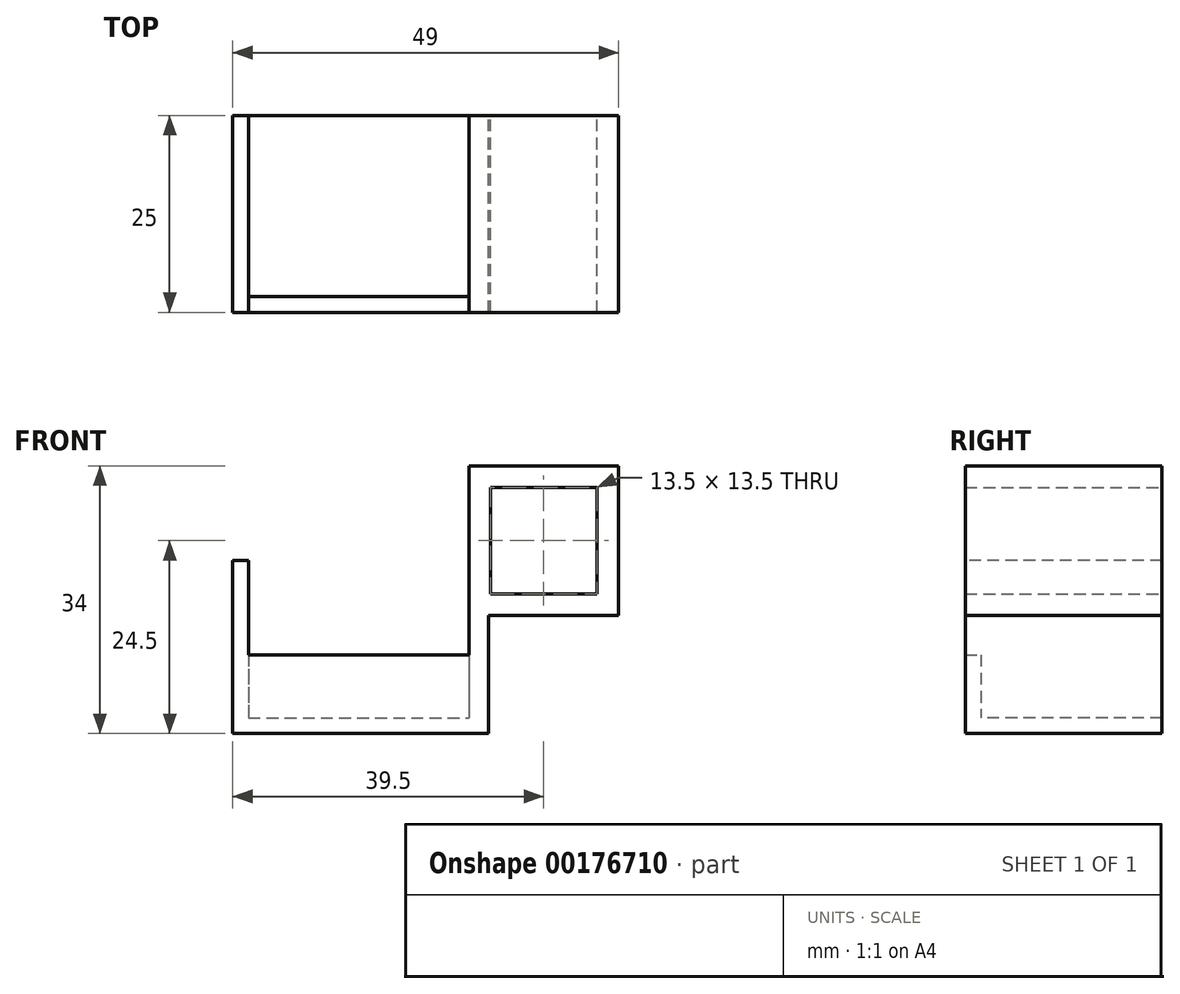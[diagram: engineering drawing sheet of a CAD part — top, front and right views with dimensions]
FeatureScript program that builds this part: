
annotation { "Feature Type Name" : "Feature", "Feature Type Description" : "" }
export const myFeature = defineFeature(function(context is Context, id is Id, definition is map)
    precondition{}
    {
        {
            var Q0;
            Q0=qCreatedBy(makeId("Front.planeOp"),FACE);
            var sketch = newSketch(context, id + "F0", { "sketchPlane" : qUnion([Q0])});
            skLineSegment(sketch, "E0.bottom", {"start": v(9.5, 9.5) * mm, "end": v(-9.5, 9.5) * mm});
            skLineSegment(sketch, "E0.top", {"start": v(9.5, -9.5) * mm, "end": v(-9.5, -9.5) * mm});
            skLineSegment(sketch, "E0.left", {"start": v(9.5, 9.5) * mm, "end": v(9.5, -9.5) * mm});
            skLineSegment(sketch, "E0.right", {"start": v(-9.5, 9.5) * mm, "end": v(-9.5, -9.5) * mm});
            skPoint(sketch, "E0.middle", {"position": v(0, 0) * mm});
            skLineSegment(sketch, "E1.bottom", {"start": v(6.75, 6.75) * mm, "end": v(-6.75, 6.75) * mm});
            skLineSegment(sketch, "E1.top", {"start": v(6.75, -6.75) * mm, "end": v(-6.75, -6.75) * mm});
            skLineSegment(sketch, "E1.left", {"start": v(6.75, 6.75) * mm, "end": v(6.75, -6.75) * mm});
            skLineSegment(sketch, "E1.right", {"start": v(-6.75, 6.75) * mm, "end": v(-6.75, -6.75) * mm});
            skSolve(sketch);
        }
        {
            var Q0;
            Q0 = qSketchRegion(id + "F0", true);
            extrude(context, id + "F1", {"entities" : qUnion([Q0]), "endBound" : BoundingType.SYMMETRIC, "depth" : 25 * mm});
        }
        {
            var Q0;
            Q0=makeQuery(id+"F1.opExtrude","SWEPT_FACE",FACE,{"disambiguationData":[OSD([sQuery(id+"F0.wireOp",EDGE,"E0.right")])]});
            var sketch = newSketch(context, id + "F2", { "sketchPlane" : qUnion([Q0])});
            skLineSegment(sketch, "E2.bottom", {"start": v(-12.5, 9.5) * mm, "end": v(12.5, 9.5) * mm});
            skLineSegment(sketch, "E2.top", {"start": v(-12.5, -24.5) * mm, "end": v(12.5, -24.5) * mm});
            skLineSegment(sketch, "E2.left", {"start": v(-12.5, 9.5) * mm, "end": v(-12.5, -24.5) * mm});
            skLineSegment(sketch, "E2.right", {"start": v(12.5, 9.5) * mm, "end": v(12.5, -24.5) * mm});
            skSolve(sketch);
        }
        {
            var Q0;
            Q0 = qSketchRegion(id + "F2", true);
            extrude(context, id + "F3", {"entities" : qUnion([Q0]), "operationType" : NewBodyOperationType.ADD, "oppositeDirection" : true, "depth" : 2.5 * mm});
        }
        {
            var Q0;
            Q0=makeQuery(id+"F3.boolean.opBoolean","MERGE",FACE,{"derivedFrom":[makeQuery(id+"F1.opExtrude","SWEPT_FACE",FACE,{"disambiguationData":[OSD([sQuery(id+"F0.wireOp",EDGE,"E0.right")])]}),makeQuery(id+"F3.opExtrude","CAP_FACE",FACE,{"disambiguationData":[OSD([sQuery(id+"F2.wireOp",EDGE,"E2.bottom"),sQuery(id+"F2.wireOp",EDGE,"E2.top"),sQuery(id+"F2.wireOp",EDGE,"E2.left"),sQuery(id+"F2.wireOp",EDGE,"E2.right")])],"isStart":true})]});
            var sketch = newSketch(context, id + "F4", { "sketchPlane" : qUnion([Q0])});
            skLineSegment(sketch, "E3.bottom", {"start": v(-12.5, -24.5) * mm, "end": v(12.5, -24.5) * mm});
            skLineSegment(sketch, "E3.top", {"start": v(-12.5, -22.5) * mm, "end": v(12.5, -22.5) * mm});
            skLineSegment(sketch, "E3.left", {"start": v(-12.5, -24.5) * mm, "end": v(-12.5, -22.5) * mm});
            skLineSegment(sketch, "E3.right", {"start": v(12.5, -24.5) * mm, "end": v(12.5, -22.5) * mm});
            skSolve(sketch);
        }
        {
            var Q0;
            Q0 = qSketchRegion(id + "F4", true);
            extrude(context, id + "F5", {"entities" : qUnion([Q0]), "operationType" : NewBodyOperationType.ADD, "depth" : 30 * mm});
        }
        {
            var Q0;
            Q0=makeQuery(id+"F5.opExtrude","SWEPT_FACE",FACE,{"disambiguationData":[OSD([sQuery(id+"F4.wireOp",EDGE,"E3.top")])]});
            var sketch = newSketch(context, id + "F6", { "sketchPlane" : qUnion([Q0])});
            skLineSegment(sketch, "E4.bottom", {"start": v(-39.5, 12.5) * mm, "end": v(-37.5, 12.5) * mm});
            skLineSegment(sketch, "E4.top", {"start": v(-39.5, -12.5) * mm, "end": v(-37.5, -12.5) * mm});
            skLineSegment(sketch, "E4.left", {"start": v(-39.5, 12.5) * mm, "end": v(-39.5, -12.5) * mm});
            skLineSegment(sketch, "E4.right", {"start": v(-37.5, 12.5) * mm, "end": v(-37.5, -12.5) * mm});
            skSolve(sketch);
        }
        {
            var Q0;
            Q0 = qSketchRegion(id + "F6", true);
            extrude(context, id + "F7", {"entities" : qUnion([Q0]), "operationType" : NewBodyOperationType.ADD, "depth" : 20 * mm});
        }
        {
            var Q0;
            Q0=makeQuery(id+"F7.boolean.opBoolean","MERGE",FACE,{"derivedFrom":[makeQuery(id+"F5.boolean.opBoolean","MERGE",FACE,{"derivedFrom":[makeQuery(id+"F3.boolean.opBoolean","MERGE",FACE,{"derivedFrom":[makeQuery(id+"F1.opExtrude","CAP_FACE",FACE,{"disambiguationData":[OSD([sQuery(id+"F0.wireOp",EDGE,"E0.bottom"),sQuery(id+"F0.wireOp",EDGE,"E0.top"),sQuery(id+"F0.wireOp",EDGE,"E0.left"),sQuery(id+"F0.wireOp",EDGE,"E0.right"),sQuery(id+"F0.wireOp",EDGE,"E1.bottom"),sQuery(id+"F0.wireOp",EDGE,"E1.top"),sQuery(id+"F0.wireOp",EDGE,"E1.left"),sQuery(id+"F0.wireOp",EDGE,"E1.right")])],"isStart":false}),makeQuery(id+"F3.opExtrude","SWEPT_FACE",FACE,{"disambiguationData":[OSD([sQuery(id+"F2.wireOp",EDGE,"E2.right")])]})]}),makeQuery(id+"F5.opExtrude","SWEPT_FACE",FACE,{"disambiguationData":[OSD([sQuery(id+"F4.wireOp",EDGE,"E3.right")])]})]}),makeQuery(id+"F7.opExtrude","SWEPT_FACE",FACE,{"disambiguationData":[OSD([sQuery(id+"F6.wireOp",EDGE,"E4.top")])]})]});
            var sketch = newSketch(context, id + "F8", { "sketchPlane" : qUnion([Q0])});
            skLineSegment(sketch, "E5.bottom", {"start": v(-39.5, -24.5) * mm, "end": v(-7, -24.5) * mm});
            skLineSegment(sketch, "E5.top", {"start": v(-39.5, -14.5) * mm, "end": v(-7, -14.5) * mm});
            skLineSegment(sketch, "E5.left", {"start": v(-39.5, -24.5) * mm, "end": v(-39.5, -14.5) * mm});
            skLineSegment(sketch, "E5.right", {"start": v(-7, -24.5) * mm, "end": v(-7, -14.5) * mm});
            skSolve(sketch);
        }
        {
            var Q0;
            Q0 = qSketchRegion(id + "F8", true);
            extrude(context, id + "F9", {"entities" : qUnion([Q0]), "operationType" : NewBodyOperationType.ADD, "oppositeDirection" : true, "depth" : 2 * mm});
        }
    });
